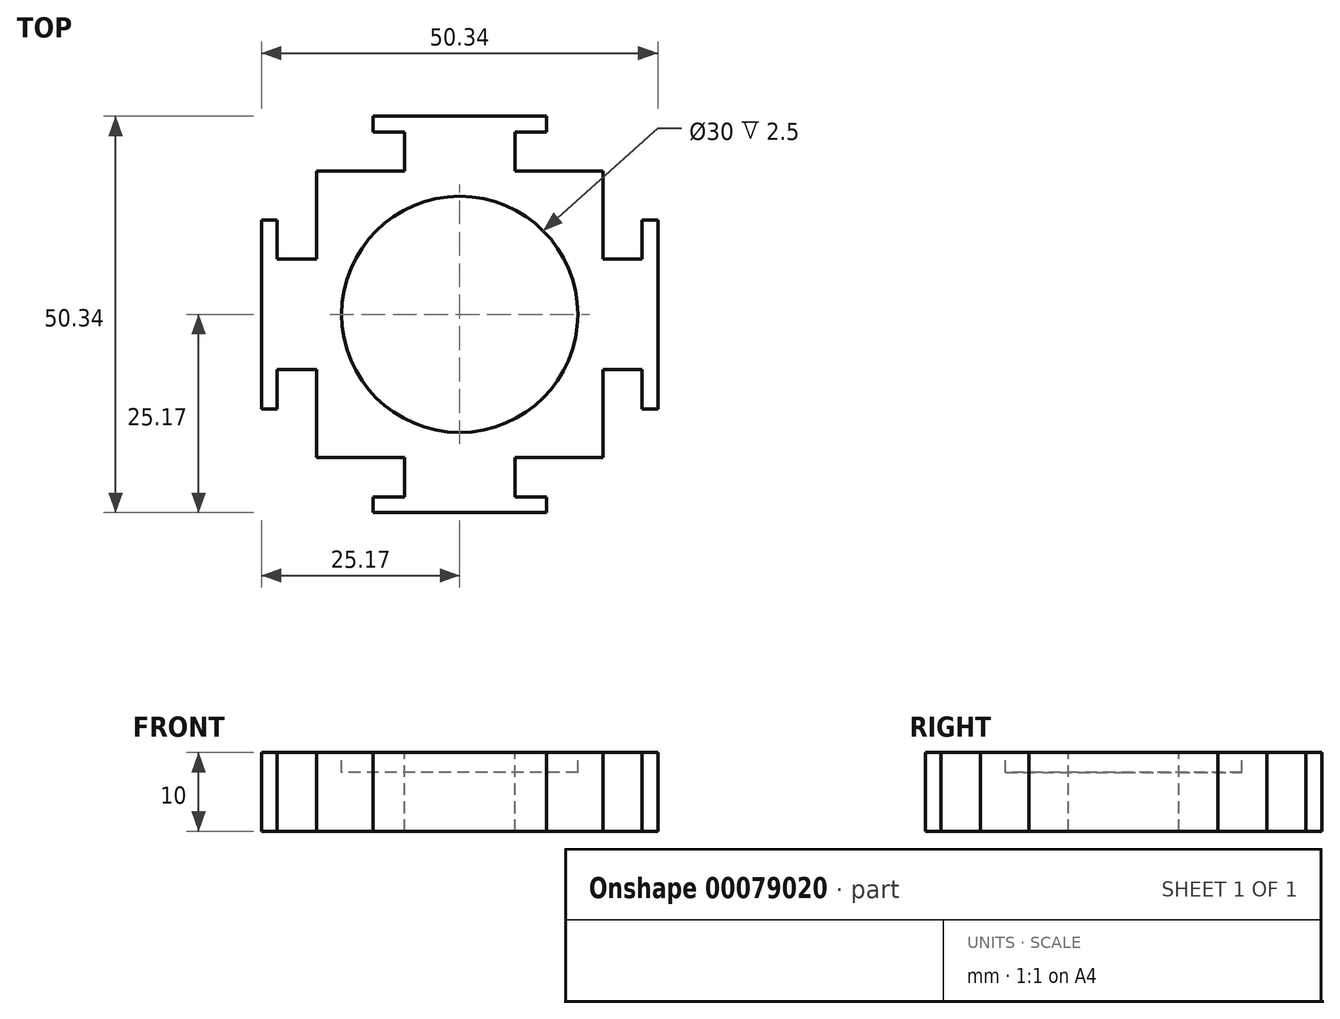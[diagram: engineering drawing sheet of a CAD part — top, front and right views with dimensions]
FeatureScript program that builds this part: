
annotation { "Feature Type Name" : "Feature", "Feature Type Description" : "" }
export const myFeature = defineFeature(function(context is Context, id is Id, definition is map)
    precondition{}
    {
        {
            var Q0;
            Q0=qCreatedBy(makeId("Top.planeOp"),FACE);
            var sketch = newSketch(context, id + "F0", { "sketchPlane" : qUnion([Q0])});
            skLineSegment(sketch, "E0.bottom", {"start": v(0, 18.17) * mm, "end": v(-18.17, 18.17) * mm});
            skPoint(sketch, "E0.middle", {"position": v(0, 0) * mm});
            skLineSegment(sketch, "E1.MirrorCS", {"start": v(-18.17, 0) * mm, "end": v(-18.17, 18.17) * mm});
            skPoint(sketch, "E2", {"position": v(-18.17, 0) * mm});
            skLineSegment(sketch, "E3", {"start": v(0, 18.17) * mm, "end": v(0, 0) * mm});
            skLineSegment(sketch, "E4", {"start": v(-18.17, 0) * mm, "end": v(0, 0) * mm});
            skPoint(sketch, "E5.orphan", {"position": v(-18.17, -18.17) * mm});
            skPoint(sketch, "E0.left.end.orphan", {"position": v(18.17, -18.17) * mm});
            skPoint(sketch, "E0.left.start.orphan", {"position": v(18.17, 18.17) * mm});
            skLineSegment(sketch, "E6", {"start": v(-18.17, 7) * mm, "end": v(-23.17, 7) * mm});
            skLineSegment(sketch, "E7", {"start": v(-23.17, 7) * mm, "end": v(-23.17, 0) * mm});
            skLineSegment(sketch, "E8", {"start": v(-23.17, 7) * mm, "end": v(-23.17, 12) * mm});
            skLineSegment(sketch, "E9", {"start": v(-23.17, 12) * mm, "end": v(-25.17, 12) * mm});
            skLineSegment(sketch, "E10", {"start": v(-25.17, 12) * mm, "end": v(-25.17, 0) * mm});
            skLineSegment(sketch, "E11", {"start": v(-25.17, 0) * mm, "end": v(-18.17, 0) * mm});
            skLineSegment(sketch, "E12", {"start": v(0, 18.17) * mm, "end": v(0, 25.17) * mm});
            skLineSegment(sketch, "E13", {"start": v(0, 25.17) * mm, "end": v(-11, 25.17) * mm});
            skLineSegment(sketch, "E14", {"start": v(-11, 25.17) * mm, "end": v(-11, 23.17) * mm});
            skLineSegment(sketch, "E15", {"start": v(-11, 23.17) * mm, "end": v(0, 23.17) * mm});
            skLineSegment(sketch, "E16", {"start": v(-7, 23.17) * mm, "end": v(-7, 18.17) * mm});
            skSolve(sketch);
        }
        {
            var Q0;
            Q0 = qSketchRegion(id + "F0", true);
            extrude(context, id + "F1", {"entities" : qUnion([Q0]), "oppositeDirection" : true, "depth" : 10 * mm});
        }
        {
            var Q0;
            Q0=makeQuery(id+"F1.opExtrude","CAP_FACE",FACE,{"disambiguationData":[OSD([sQuery(id+"F0.wireOp",EDGE,"E0.bottom"),sQuery(id+"F0.wireOp",EDGE,"UIb6YOiN-wxSo-lSF2-kpko-APr7q6lGE7w8"),sQuery(id+"F0.wireOp",EDGE,"7sIu6wZ2-w2ZO-qvAv-kVXd-9A4nwvC2tgGi.bottom"),sQuery(id+"F0.wireOp",EDGE,"7sIu6wZ2-w2ZO-qvAv-kVXd-9A4nwvC2tgGi.top"),sQuery(id+"F0.wireOp",EDGE,"7sIu6wZ2-w2ZO-qvAv-kVXd-9A4nwvC2tgGi.left"),sQuery(id+"F0.wireOp",EDGE,"E1.MirrorCS"),sQuery(id+"F0.wireOp",EDGE,"XQsER0wi-Vg6o-c3ds-G2QR-Lw313FhJWP8Z"),sQuery(id+"F0.wireOp",EDGE,"E3"),sQuery(id+"F0.wireOp",EDGE,"E4"),sQuery(id+"F0.wireOp",EDGE,"E6"),sQuery(id+"F0.wireOp",EDGE,"E8"),sQuery(id+"F0.wireOp",EDGE,"E9"),sQuery(id+"F0.wireOp",EDGE,"E10"),sQuery(id+"F0.wireOp",EDGE,"E11")])],"isStart":true});
            var sketch = newSketch(context, id + "F2", { "sketchPlane" : qUnion([Q0])});
            skArc(sketch, "E17", {"start": v(0, 15) * mm, "mid": v(-10.6, 10.6) * mm, "end": v(-15, 0) * mm});
            skPoint(sketch, "E18", {"position": v(0, 15) * mm});
            skPoint(sketch, "E19", {"position": v(-15, 0) * mm});
            skLineSegment(sketch, "E20", {"start": v(0, 15) * mm, "end": v(0, 0) * mm});
            skLineSegment(sketch, "E21", {"start": v(0, 0) * mm, "end": v(-15, 0) * mm});
            skSolve(sketch);
        }
        {
            var Q0;
            Q0 = qSketchRegion(id + "F2", true);
            extrude(context, id + "F3", {"entities" : qUnion([Q0]), "operationType" : NewBodyOperationType.REMOVE, "oppositeDirection" : true, "depth" : 2.5 * mm});
        }
        {
            var Q0;
            Q0=makeQuery(id+"F1.opExtrude","SWEPT_BODY",BODY,{"disambiguationData":[OSD([sQuery(id+"F0.wireOp",EDGE,"E0.bottom"),sQuery(id+"F0.wireOp",EDGE,"UIb6YOiN-wxSo-lSF2-kpko-APr7q6lGE7w8"),sQuery(id+"F0.wireOp",EDGE,"7sIu6wZ2-w2ZO-qvAv-kVXd-9A4nwvC2tgGi.bottom"),sQuery(id+"F0.wireOp",EDGE,"7sIu6wZ2-w2ZO-qvAv-kVXd-9A4nwvC2tgGi.top"),sQuery(id+"F0.wireOp",EDGE,"7sIu6wZ2-w2ZO-qvAv-kVXd-9A4nwvC2tgGi.left"),sQuery(id+"F0.wireOp",EDGE,"E1.MirrorCS"),sQuery(id+"F0.wireOp",EDGE,"XQsER0wi-Vg6o-c3ds-G2QR-Lw313FhJWP8Z"),sQuery(id+"F0.wireOp",EDGE,"E3"),sQuery(id+"F0.wireOp",EDGE,"E4")])]});
            var Q1;
            Q1=qCreatedBy(makeId("Right.planeOp"),FACE);
            mirror(context, id + "F4", {"operationType" : NewBodyOperationType.ADD, "entities" : qUnion([Q0]), "mirrorPlane" : qUnion([Q1])});
        }
        {
            var Q0;
            Q0=makeQuery(id+"F1.opExtrude","SWEPT_BODY",BODY,{"disambiguationData":[OSD([sQuery(id+"F0.wireOp",EDGE,"E0.bottom"),sQuery(id+"F0.wireOp",EDGE,"UIb6YOiN-wxSo-lSF2-kpko-APr7q6lGE7w8"),sQuery(id+"F0.wireOp",EDGE,"7sIu6wZ2-w2ZO-qvAv-kVXd-9A4nwvC2tgGi.bottom"),sQuery(id+"F0.wireOp",EDGE,"7sIu6wZ2-w2ZO-qvAv-kVXd-9A4nwvC2tgGi.top"),sQuery(id+"F0.wireOp",EDGE,"7sIu6wZ2-w2ZO-qvAv-kVXd-9A4nwvC2tgGi.left"),sQuery(id+"F0.wireOp",EDGE,"E1.MirrorCS"),sQuery(id+"F0.wireOp",EDGE,"XQsER0wi-Vg6o-c3ds-G2QR-Lw313FhJWP8Z"),sQuery(id+"F0.wireOp",EDGE,"E3"),sQuery(id+"F0.wireOp",EDGE,"E4")])]});
            var Q1;
            Q1=qCreatedBy(makeId("Front.planeOp"),FACE);
            mirror(context, id + "F5", {"operationType" : NewBodyOperationType.ADD, "entities" : qUnion([Q0]), "mirrorPlane" : qUnion([Q1])});
        }
    });
